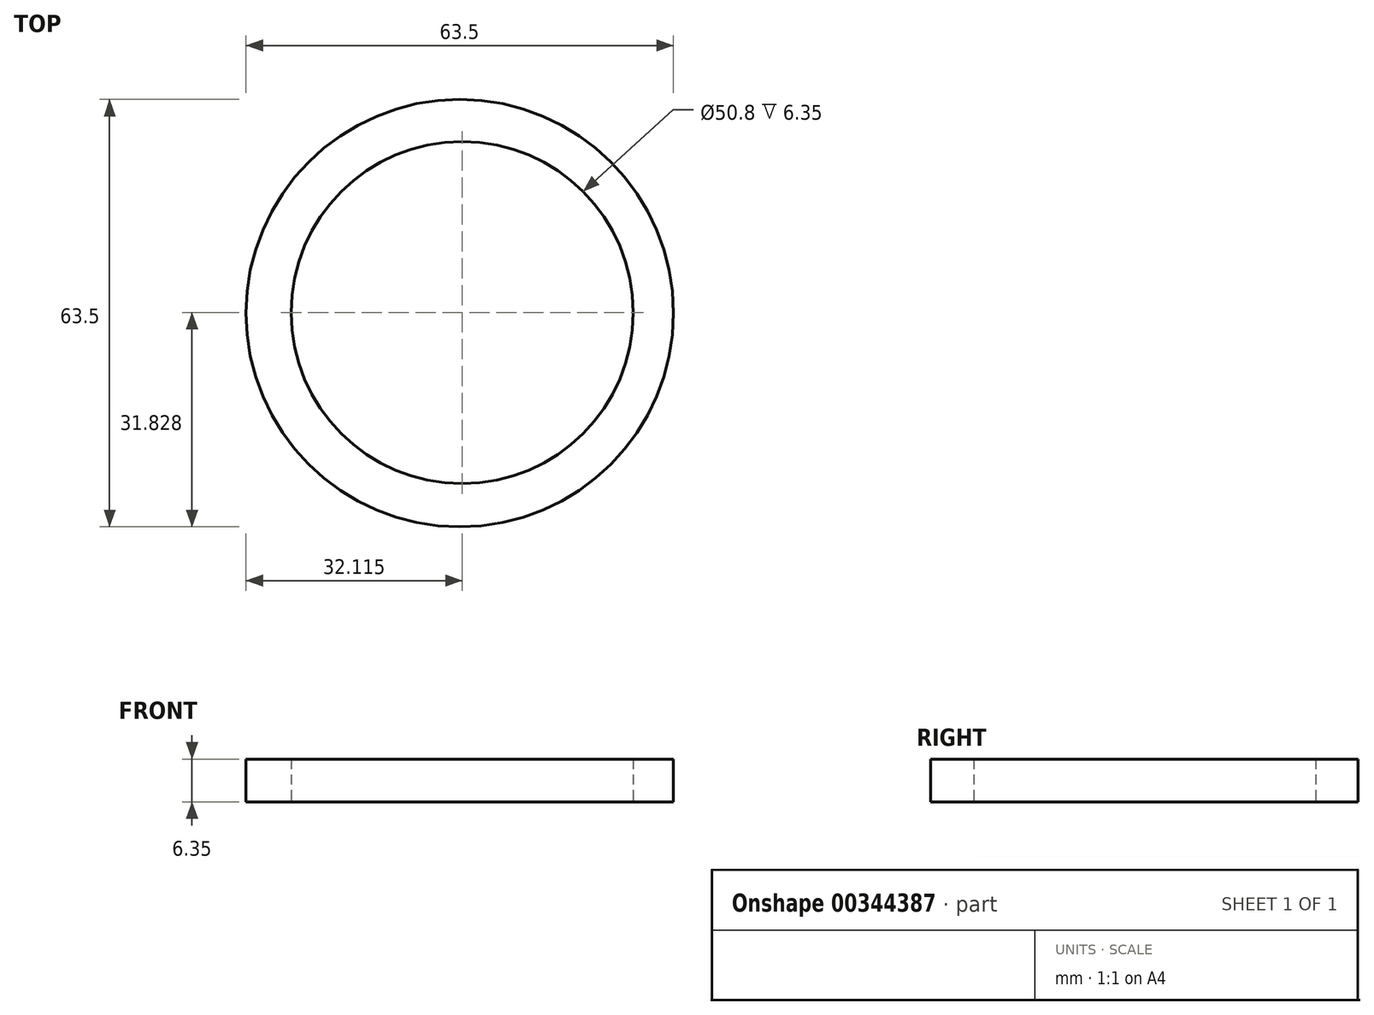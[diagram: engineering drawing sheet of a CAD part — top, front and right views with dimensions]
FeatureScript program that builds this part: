
annotation { "Feature Type Name" : "Feature", "Feature Type Description" : "" }
export const myFeature = defineFeature(function(context is Context, id is Id, definition is map)
    precondition{}
    {
        {
            var Q0;
            Q0=qCreatedBy(makeId("Top.planeOp"),FACE);
            var sketch = newSketch(context, id + "F0", { "sketchPlane" : qUnion([Q0])});
            skCircle(sketch, "E0", {"center": v(-38.7, 39.12) * mm, "radius": 31.75 * mm});
            skSolve(sketch);
        }
        {
            var Q0;
            Q0=makeQuery(id+"F0.imprint","IMPRINT",FACE,{"disambiguationData":[TD([[makeQuery(id+"F0.imprint","IMPRINT",EDGE,{"derivedFrom":sQuery(id+"F0.wireOp",EDGE,"E0")}),1.0]])]});
            extrude(context, id + "F1", {"entities" : qUnion([Q0]), "depth" : 6.35 * mm});
        }
        {
            var Q0;
            Q0=qCreatedBy(makeId("Top.planeOp"),FACE);
            var sketch = newSketch(context, id + "F2", { "sketchPlane" : qUnion([Q0])});
            skCircle(sketch, "E1", {"center": v(-38.35, 39.2) * mm, "radius": 25.4 * mm});
            skSolve(sketch);
        }
        {
            var Q0;
            Q0 = qSketchRegion(id + "F2", true);
            extrude(context, id + "F3", {"entities" : qUnion([Q0]), "operationType" : NewBodyOperationType.REMOVE, "endBound" : BoundingType.UP_TO_NEXT, "depth" : 6.35 * mm});
        }
    });
